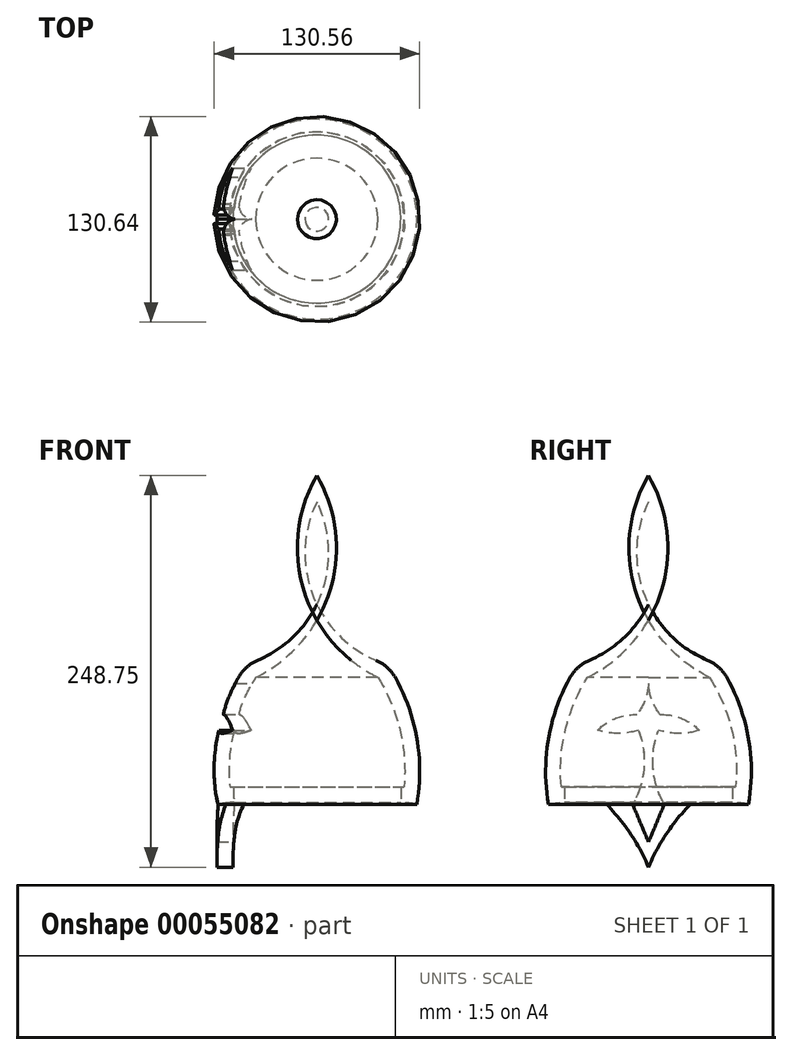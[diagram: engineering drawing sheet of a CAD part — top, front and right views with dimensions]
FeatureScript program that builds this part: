
annotation { "Feature Type Name" : "Feature", "Feature Type Description" : "" }
export const myFeature = defineFeature(function(context is Context, id is Id, definition is map)
    precondition{}
    {
        {
            var Q0;
            Q0=qCreatedBy(makeId("Front.planeOp"),FACE);
            var sketch = newSketch(context, id + "F0", { "sketchPlane" : qUnion([Q0])});
            skArc(sketch, "E0", {"start": v(-44.72, 88.9) * mm, "mid": v(-62.68, 46.26) * mm, "end": v(-63.5, 0) * mm});
            skLineSegment(sketch, "E1", {"start": v(0, 116.84) * mm, "end": v(0, 127) * mm});
            skArc(sketch, "E2", {"start": v(-44.72, 88.9) * mm, "mid": v(-18.41, 103.32) * mm, "end": v(0, 127) * mm});
            skArc(sketch, "E3", {"start": v(0, -11.8) * mm, "mid": v(-30.64, 0.04) * mm, "end": v(-63.5, 0) * mm});
            skLineSegment(sketch, "E4", {"start": v(0, -11.8) * mm, "end": v(0, 0) * mm});
            skLineSegment(sketch, "E5", {"start": v(-44.72, 88.9) * mm, "end": v(-38.78, 80.65) * mm});
            skLineSegment(sketch, "E6", {"start": v(0, 127) * mm, "end": v(0, 116.84) * mm});
            skArc(sketch, "E7", {"start": v(-38.78, 80.65) * mm, "mid": v(-16.71, 95.88) * mm, "end": v(0, 116.84) * mm});
            skArc(sketch, "E8", {"start": v(-38.78, 80.65) * mm, "mid": v(-52.8, 47.17) * mm, "end": v(-55.38, 10.96) * mm});
            skArc(sketch, "E9", {"start": v(0, -2.99) * mm, "mid": v(-26.65, 8.1) * mm, "end": v(-55.38, 10.96) * mm});
            skSolve(sketch);
        }
        {
            var Q0;
            Q0 = qSketchRegion(id + "F0", true);
            var Q1;
            Q1=sQuery(id+"F0.wireOp",EDGE,"E6");
            revolve(context, id + "F1", {"entities" : qUnion([Q0]), "axis" : qUnion([Q1]), "revolveType" : RevolveType.FULL});
        }
        {
            var Q0;
            Q0=qCreatedBy(makeId("Right.planeOp"),FACE);
            var sketch = newSketch(context, id + "F2", { "sketchPlane" : qUnion([Q0])});
            skLineSegment(sketch, "E10.0", {"start": v(-44.72, 88.9) * mm, "end": v(44.72, 88.9) * mm});
            skLineSegment(sketch, "E11.0", {"start": v(-63.5, 0) * mm, "end": v(63.5, 0) * mm});
            skArc(sketch, "E12", {"start": v(-10.05, 0) * mm, "mid": v(-2.9, 23.13) * mm, "end": v(-6.38, 47.1) * mm});
            skArc(sketch, "E13", {"start": v(-32.38, 47.1) * mm, "mid": v(-19.38, 45.07) * mm, "end": v(-6.38, 47.1) * mm});
            skArc(sketch, "E14", {"start": v(-7.43, 57.07) * mm, "mid": v(-20.9, 54.59) * mm, "end": v(-32.38, 47.1) * mm});
            skArc(sketch, "E15", {"start": v(-7.43, 57.07) * mm, "mid": v(-2.17, 66.34) * mm, "end": v(0, 76.77) * mm});
            skLineSegment(sketch, "E16", {"start": v(0, 76.77) * mm, "end": v(0, 48.67) * mm});
            skArc(sketch, "E17.MirrorCS", {"start": v(7.43, 57.07) * mm, "mid": v(2.17, 66.34) * mm, "end": v(0, 76.77) * mm});
            skArc(sketch, "E18.MirrorCS", {"start": v(7.43, 57.07) * mm, "mid": v(20.9, 54.59) * mm, "end": v(32.38, 47.1) * mm});
            skArc(sketch, "E19.MirrorCS", {"start": v(32.38, 47.1) * mm, "mid": v(19.38, 45.07) * mm, "end": v(6.38, 47.1) * mm});
            skArc(sketch, "E20.MirrorCS", {"start": v(10.05, 0) * mm, "mid": v(2.9, 23.13) * mm, "end": v(6.38, 47.1) * mm});
            skLineSegment(sketch, "E21", {"start": v(10.05, 0) * mm, "end": v(0, -5.07) * mm});
            skLineSegment(sketch, "E22", {"start": v(0, -5.07) * mm, "end": v(-10.05, 0) * mm});
            skSolve(sketch);
        }
        {
            var Q0;
            Q0 = qSketchRegion(id + "F2", true);
            extrude(context, id + "F3", {"entities" : qUnion([Q0]), "operationType" : NewBodyOperationType.REMOVE, "oppositeDirection" : true, "depth" : 127 * mm});
        }
        {
            var Q0;
            Q0=qCreatedBy(makeId("Top.planeOp"),FACE);
            var sketch = newSketch(context, id + "F4", { "sketchPlane" : qUnion([Q0])});
            skArc(sketch, "E23.0", {"start": v(-52.67, -8.44) * mm, "mid": v(53.34, 0) * mm, "end": v(-52.67, 8.44) * mm});
            skFitSpline(sketch, "E24.0", {"points": [v(0, 9.05) * mm, v(-1.13, 9.05) * mm, v(-2.29, 9) * mm, v(-3.5, 8.92) * mm, v(-4.52, 8.85) * mm, v(-5.66, 8.74) * mm, v(-6.91, 8.59) * mm, v(-7.81, 8.48) * mm, v(-8.94, 8.33) * mm, v(-10.28, 8.15) * mm, v(-10.67, 8.1) * mm, v(-11.23, 8.02) * mm, v(-11.96, 7.91) * mm, v(-12.73, 7.8) * mm, v(-13.29, 7.73) * mm, v(-13.63, 7.68) * mm, v(-14.88, 7.5) * mm, v(-16, 7.35) * mm, v(-16.97, 7.23) * mm, v(-18.12, 7.08) * mm, v(-19.24, 6.94) * mm, v(-20.32, 6.81) * mm, v(-22.58, 6.55) * mm, v(-24.84, 6.33) * mm, v(-27.1, 6.14) * mm, v(-31.5, 5.76) * mm, v(-36.13, 5.5) * mm, v(-41, 5.36) * mm, v(-43.32, 5.29) * mm, v(-45.67, 5.24) * mm, v(-48.06, 5.23) * mm, v(-50.43, 5.2) * mm, v(-52.78, 5.22) * mm, v(-55.13, 5.25) * mm]});
            skFitSpline(sketch, "E25.0", {"points": [v(0, -9.05) * mm, v(-1.13, -9.05) * mm, v(-2.29, -9) * mm, v(-3.5, -8.92) * mm, v(-4.52, -8.85) * mm, v(-5.66, -8.74) * mm, v(-6.91, -8.59) * mm, v(-7.81, -8.48) * mm, v(-8.94, -8.33) * mm, v(-10.28, -8.15) * mm, v(-10.67, -8.1) * mm, v(-11.23, -8.02) * mm, v(-11.96, -7.91) * mm, v(-12.73, -7.8) * mm, v(-13.29, -7.73) * mm, v(-13.63, -7.68) * mm, v(-14.88, -7.5) * mm, v(-16, -7.35) * mm, v(-16.97, -7.23) * mm, v(-18.12, -7.08) * mm, v(-19.24, -6.94) * mm, v(-20.32, -6.81) * mm, v(-22.58, -6.55) * mm, v(-24.84, -6.33) * mm, v(-27.1, -6.14) * mm, v(-31.5, -5.76) * mm, v(-36.13, -5.5) * mm, v(-41, -5.36) * mm, v(-43.32, -5.29) * mm, v(-45.67, -5.24) * mm, v(-48.06, -5.23) * mm, v(-50.43, -5.2) * mm, v(-52.78, -5.22) * mm, v(-55.13, -5.25) * mm]});
            skCircle(sketch, "E26", {"center": v(0, 0) * mm, "radius": 53.34 * mm});
            skSolve(sketch);
        }
        {
            var Q0;
            Q0 = qSketchRegion(id + "F4", true);
            extrude(context, id + "F5", {"entities" : qUnion([Q0]), "operationType" : NewBodyOperationType.REMOVE, "depth" : 18.43 * mm, "hasSecondDirection" : true, "secondDirectionOppositeDirection" : true, "secondDirectionDepth" : 25.4 * mm});
        }
        {
            var Q0;
            Q0=qCreatedBy(makeId("Right.planeOp"),FACE);
            cPlane(context, id + "F6", {"entities" : qUnion([Q0]), "cplaneType" : CPlaneType.OFFSET, "offset" : 50.8 * mm, "oppositeDirection" : true, "width" : 152.4 * mm, "height" : 152.4 * mm});
        }
        {
            var Q0;
            Q0=qCreatedBy(id+"F6.planeOp",FACE);
            var sketch = newSketch(context, id + "F7", { "sketchPlane" : qUnion([Q0])});
            skArc(sketch, "E27.0", {"start": v(5.23, 11.04) * mm, "mid": v(7.04, 6.08) * mm, "end": v(9.32, 1.32) * mm});
            skArc(sketch, "E28.0", {"start": v(6.38, 47.1) * mm, "mid": v(2.9, 23.13) * mm, "end": v(10.05, 0) * mm});
            skArc(sketch, "E29.0", {"start": v(-6.38, 47.1) * mm, "mid": v(-2.9, 23.13) * mm, "end": v(-10.05, 0) * mm});
            skLineSegment(sketch, "E30.0", {"start": v(-63.5, 0) * mm, "end": v(-10.05, 0) * mm});
            skLineSegment(sketch, "E31", {"start": v(10.05, 0) * mm, "end": v(0, -23.99) * mm});
            skLineSegment(sketch, "E32", {"start": v(0, -23.99) * mm, "end": v(-10.05, 0) * mm});
            skLineSegment(sketch, "E33", {"start": v(0, -23.99) * mm, "end": v(0, -11.7) * mm});
            skArc(sketch, "E34", {"start": v(26.66, 0) * mm, "mid": v(11.43, -18.68) * mm, "end": v(0, -39.9) * mm});
            skArc(sketch, "E35.MirrorCS", {"start": v(-26.66, 0) * mm, "mid": v(-11.43, -18.68) * mm, "end": v(0, -39.9) * mm});
            skPoint(sketch, "E36.MirrorCS.end.orphan", {"position": v(0, -39.9) * mm});
            skPoint(sketch, "E37.start.orphan", {"position": v(-26.66, 0) * mm});
            skLineSegment(sketch, "E38.trimOffspring", {"start": v(10.05, 0) * mm, "end": v(63.5, 0) * mm});
            skSolve(sketch);
        }
        {
            var Q0;
            Q0 = qSketchRegion(id + "F7", true);
            extrude(context, id + "F8", {"entities" : qUnion([Q0]), "endBound" : BoundingType.SYMMETRIC, "oppositeDirection" : true, "depth" : 50.8 * mm});
        }
        {
            var Q0;
            Q0=qCreatedBy(makeId("Top.planeOp"),FACE);
            var sketch = newSketch(context, id + "F9", { "sketchPlane" : qUnion([Q0])});
            skArc(sketch, "E39.0", {"start": v(-62.7, -10.05) * mm, "mid": v(63.5, 0) * mm, "end": v(-62.7, 10.05) * mm});
            skArc(sketch, "E40.0", {"start": v(-52.52, 9.32) * mm, "mid": v(53.34, 0) * mm, "end": v(-52.52, -9.32) * mm});
            skCircle(sketch, "E41", {"center": v(0, 0) * mm, "radius": 53.34 * mm});
            skCircle(sketch, "E42", {"center": v(0, 0) * mm, "radius": 63.5 * mm});
            skCircle(sketch, "E43", {"center": v(0, 0) * mm, "radius": 84.95 * mm});
            skSolve(sketch);
        }
        {
            var Q0;
            Q0=makeQuery(id+"F9.imprint","IMPRINT",FACE,{"disambiguationData":[TD([[makeQuery(id+"F9.imprint","IMPRINT",EDGE,{"derivedFrom":sQuery(id+"F9.wireOp",EDGE,"E43")}),1.0]])]});
            var Q1;
            {var subQ0=sQuery(id+"F9.wireOp",EDGE,"E41");var subQ1=makeQuery(id+"F9.imprint","IMPRINT",VERTEX,{"disambiguationData":[OD(0.0)],"derivedFrom":subQ0});Q1=makeQuery(id+"F9.imprint","IMPRINT",FACE,{"disambiguationData":[TD([[makeQuery(id+"F9.imprint","IMPRINT",EDGE,{"disambiguationData":[TD([[subQ1,1.0]])],"derivedFrom":subQ0}),1.0]])]});}
            extrude(context, id + "F10", {"entities" : qUnion([Q0, Q1]), "operationType" : NewBodyOperationType.REMOVE, "oppositeDirection" : true, "depth" : 106 * mm});
        }
        {
            var Q0;
            Q0=makeQuery(id+"F1.opRevolve","SWEPT_EDGE",EDGE,{"disambiguationData":[OSD([sQuery(id+"F0.wireOp",EDGE,"E0"),sQuery(id+"F0.wireOp",EDGE,"E2"),sQuery(id+"F0.wireOp",EDGE,"E5")])]});
            fillet(context, id + "F11", {"entities" : qUnion([Q0]), "radius" : 25.4 * mm, "tangentPropagation" : true, "allowEdgeOverflow" : false});
        }
    });
